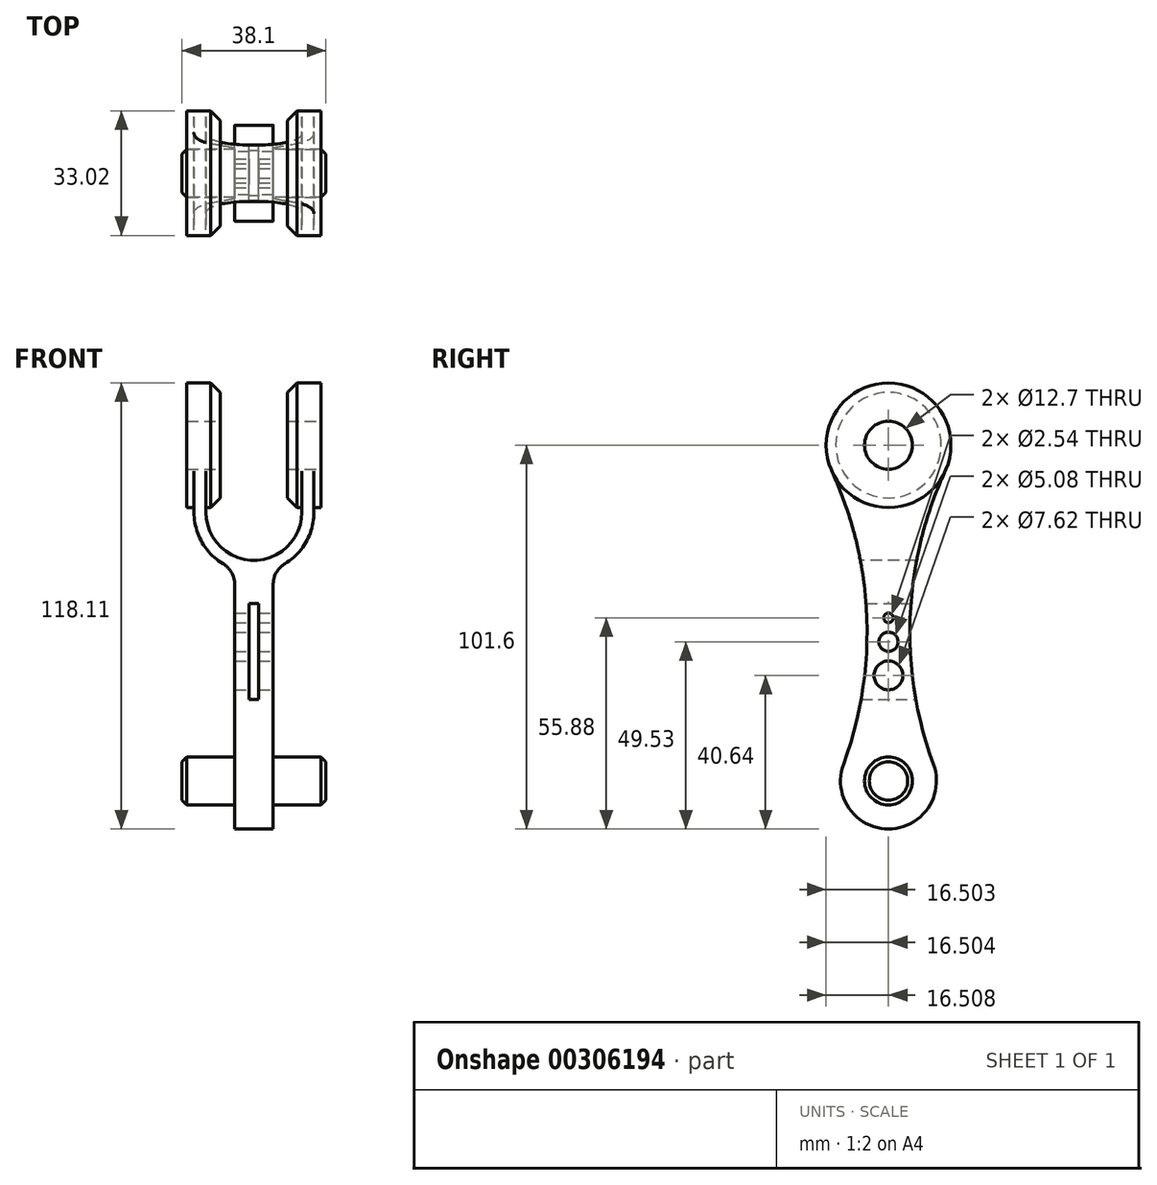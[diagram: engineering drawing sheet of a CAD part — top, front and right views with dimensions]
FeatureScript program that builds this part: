
annotation { "Feature Type Name" : "Feature", "Feature Type Description" : "" }
export const myFeature = defineFeature(function(context is Context, id is Id, definition is map)
    precondition{}
    {
        {
            var Q0;
            Q0=qCreatedBy(makeId("Front.planeOp"),FACE);
            var sketch = newSketch(context, id + "F0", { "sketchPlane" : qUnion([Q0])});
            skPoint(sketch, "E0.middle", {"position": v(0, 0) * mm});
            skArc(sketch, "E1", {"start": v(-8.17, -19.4) * mm, "mid": v(-13.82, -25.2) * mm, "end": v(-15.88, -33.02) * mm});
            skLineSegment(sketch, "E2.bottom", {"start": v(-5.08, 15.05) * mm, "end": v(5.08, 15.05) * mm});
            skLineSegment(sketch, "E2.left", {"start": v(-5.08, 15.05) * mm, "end": v(-5.08, -13.95) * mm});
            skLineSegment(sketch, "E2.right", {"start": v(5.08, 15.05) * mm, "end": v(5.08, -13.95) * mm});
            skArc(sketch, "E3", {"start": v(12.7, -33.02) * mm, "mid": v(0, -20.32) * mm, "end": v(-12.7, -33.02) * mm});
            skLineSegment(sketch, "E4.top", {"start": v(14.22, -50.8) * mm, "end": v(14.36, -50.8) * mm});
            skLineSegment(sketch, "E4.left", {"start": v(12.7, -33.02) * mm, "end": v(12.7, -49.28) * mm});
            skLineSegment(sketch, "E4.right", {"start": v(15.88, -33.02) * mm, "end": v(15.88, -49.28) * mm});
            skLineSegment(sketch, "E5.top", {"start": v(-14.36, -50.8) * mm, "end": v(-14.22, -50.8) * mm});
            skLineSegment(sketch, "E5.left", {"start": v(-15.88, -33.02) * mm, "end": v(-15.88, -49.28) * mm});
            skLineSegment(sketch, "E5.right", {"start": v(-12.7, -33.02) * mm, "end": v(-12.7, -49.28) * mm});
            skArc(sketch, "E6.trimOffspring", {"start": v(15.88, -33.02) * mm, "mid": v(13.82, -25.2) * mm, "end": v(8.17, -19.4) * mm});
            skPoint(sketch, "E7.visualSharp", {"position": v(-5.08, -17.97) * mm});
            skArc(sketch, "E7.filletArc", {"start": v(-8.17, -19.4) * mm, "mid": v(-5.9, -17.08) * mm, "end": v(-5.08, -13.95) * mm});
            skPoint(sketch, "E8.visualSharp", {"position": v(5.08, -17.97) * mm});
            skArc(sketch, "E8.filletArc", {"start": v(5.08, -13.95) * mm, "mid": v(5.9, -17.08) * mm, "end": v(8.17, -19.4) * mm});
            skArc(sketch, "E9.filletArc", {"start": v(12.7, -49.28) * mm, "mid": v(13.15, -50.35) * mm, "end": v(14.22, -50.8) * mm});
            skArc(sketch, "E10.filletArc", {"start": v(14.36, -50.8) * mm, "mid": v(15.44, -50.35) * mm, "end": v(15.88, -49.28) * mm});
            skArc(sketch, "E11.filletArc", {"start": v(-15.88, -49.28) * mm, "mid": v(-15.44, -50.35) * mm, "end": v(-14.36, -50.8) * mm});
            skArc(sketch, "E12.filletArc", {"start": v(-14.22, -50.8) * mm, "mid": v(-13.15, -50.35) * mm, "end": v(-12.7, -49.28) * mm});
            skSolve(sketch);
        }
        {
            var Q0;
            Q0=qSketchRegion(id+"F0",true);
            extrude(context, id + "F1", {"entities" : qUnion([Q0]), "depth" : 38.1 * mm, "symmetric" : true});
        }
        {
            var Q0;
            Q0=qCreatedBy(makeId("Right.planeOp"),FACE);
            var sketch = newSketch(context, id + "F2", { "sketchPlane" : qUnion([Q0])});
            skCircle(sketch, "E13", {"center": v(0, -50.8) * mm, "radius": 6.35 * mm});
            skSolve(sketch);
        }
        {
            var Q0;
            Q0=qCreatedBy(makeId("Right.planeOp"),FACE);
            var sketch = newSketch(context, id + "F3", { "sketchPlane" : qUnion([Q0])});
            skCircle(sketch, "E14", {"center": v(0, -50.8) * mm, "radius": 16.51 * mm});
            skSolve(sketch);
        }
        {
            var Q0;
            Q0=qSketchRegion(id+"F3",true);
            extrude(context, id + "F4", {"entities" : qUnion([Q0]), "operationType" : NewBodyOperationType.ADD, "depth" : 35.56 * mm, "symmetric" : true});
        }
        {
            var Q0;
            Q0=qCreatedBy(makeId("Front.planeOp"),FACE);
            var sketch = newSketch(context, id + "F5", { "sketchPlane" : qUnion([Q0])});
            skLineSegment(sketch, "E15.bottom", {"start": v(8.9, -69.85) * mm, "end": v(-8.89, -69.85) * mm});
            skLineSegment(sketch, "E15.top", {"start": v(8.9, -31.75) * mm, "end": v(-8.89, -31.75) * mm});
            skLineSegment(sketch, "E15.left", {"start": v(8.9, -69.85) * mm, "end": v(8.9, -31.75) * mm});
            skLineSegment(sketch, "E15.right", {"start": v(-8.89, -69.85) * mm, "end": v(-8.89, -31.75) * mm});
            skPoint(sketch, "E15.middle", {"position": v(0, -50.8) * mm});
            skSolve(sketch);
        }
        {
            var Q0;
            Q0=qSketchRegion(id+"F2",true);
            extrude(context, id + "F6", {"entities" : qUnion([Q0]), "operationType" : NewBodyOperationType.REMOVE, "oppositeDirection" : true, "depth" : 76.2 * mm, "symmetric" : true});
        }
        {
            var Q0;
            Q0=qSketchRegion(id+"F5",true);
            extrude(context, id + "F7", {"entities" : qUnion([Q0]), "operationType" : NewBodyOperationType.REMOVE, "oppositeDirection" : true, "depth" : 38.1 * mm, "symmetric" : true});
        }
        {
            var Q0;
            Q0=makeQuery(id+"F7.boolean.opBoolean","INTERSECT",EDGE,{"derivedFrom":[makeQuery(id+"F4.opExtrude","SWEPT_FACE",FACE,{"disambiguationData":[OSD([sQuery(id+"F3.wireOp",EDGE,"E14")])]}),makeQuery(id+"F7.opExtrude","SWEPT_FACE",FACE,{"disambiguationData":[OSD([sQuery(id+"F5.wireOp",EDGE,"E15.right")])]})]});
            var Q1;
            Q1=makeQuery(id+"F7.boolean.opBoolean","INTERSECT",EDGE,{"derivedFrom":[makeQuery(id+"F4.opExtrude","SWEPT_FACE",FACE,{"disambiguationData":[OSD([sQuery(id+"F3.wireOp",EDGE,"E14")])]}),makeQuery(id+"F7.opExtrude","SWEPT_FACE",FACE,{"disambiguationData":[OSD([sQuery(id+"F5.wireOp",EDGE,"E15.left")])]})]});
            chamfer(context, id + "F8", {"entities" : qUnion([Q0, Q1]), "width" : 2.54 * mm, "tangentPropagation" : true});
        }
        {
            var Q0;
            Q0=qCreatedBy(makeId("Right.planeOp"),FACE);
            var sketch = newSketch(context, id + "F9", { "sketchPlane" : qUnion([Q0])});
            skArc(sketch, "E16", {"start": v(19.05, 38.09) * mm, "mid": v(0, 57.15) * mm, "end": v(-19.05, 38.09) * mm});
            skLineSegment(sketch, "E17.top", {"start": v(-19.05, 12.69) * mm, "end": v(19.05, 12.69) * mm});
            skLineSegment(sketch, "E17.left", {"start": v(-19.05, 38.09) * mm, "end": v(-19.05, 12.69) * mm});
            skLineSegment(sketch, "E17.right", {"start": v(19.05, 38.09) * mm, "end": v(19.05, 12.69) * mm});
            skSolve(sketch);
        }
        {
            var Q0;
            Q0=qSketchRegion(id+"F9",true);
            extrude(context, id + "F10", {"entities" : qUnion([Q0]), "operationType" : NewBodyOperationType.ADD, "depth" : 10.16 * mm, "symmetric" : true});
        }
        {
            var Q0;
            Q0=qCreatedBy(makeId("Right.planeOp"),FACE);
            var sketch = newSketch(context, id + "F11", { "sketchPlane" : qUnion([Q0])});
            skCircle(sketch, "E18", {"center": v(0, 38.1) * mm, "radius": 6.35 * mm});
            skSolve(sketch);
        }
        {
            var Q0;
            Q0=qSketchRegion(id+"F11",true);
            extrude(context, id + "F12", {"entities" : qUnion([Q0]), "operationType" : NewBodyOperationType.ADD, "depth" : 38.1 * mm, "symmetric" : true});
        }
        {
            var Q0;
            Q0=makeQuery(id+"F12.opExtrude","CAP_EDGE",EDGE,{"disambiguationData":[OSD([sQuery(id+"F11.wireOp",EDGE,"E18")])],"isStart":true});
            var Q1;
            Q1=makeQuery(id+"F12.opExtrude","CAP_EDGE",EDGE,{"disambiguationData":[OSD([sQuery(id+"F11.wireOp",EDGE,"E18")])],"isStart":false});
            chamfer(context, id + "F13", {"entities" : qUnion([Q0, Q1]), "width" : 1.27 * mm, "tangentPropagation" : true});
        }
        {
            var Q0;
            Q0=qCreatedBy(makeId("Right.planeOp"),FACE);
            var sketch = newSketch(context, id + "F14", { "sketchPlane" : qUnion([Q0])});
            skArc(sketch, "E19", {"start": v(11.92, 33.71) * mm, "mid": v(0, 50.8) * mm, "end": v(-11.92, 33.71) * mm});
            skArc(sketch, "E20", {"start": v(-15, -43.9) * mm, "mid": v(0, -67.31) * mm, "end": v(15, -43.9) * mm});
            skArc(sketch, "E21", {"start": v(11.92, 33.71) * mm, "mid": v(5.75, -5.4) * mm, "end": v(15, -43.9) * mm});
            skPoint(sketch, "E22.center.orphan", {"position": v(45.72, -6.35) * mm});
            skPoint(sketch, "E23.center.orphan", {"position": v(-45.72, -6.35) * mm});
            skArc(sketch, "E24", {"start": v(-15, -43.9) * mm, "mid": v(-5.75, -5.4) * mm, "end": v(-11.92, 33.71) * mm});
            skSolve(sketch);
        }
        {
            var Q0;
            Q0=qSketchRegion(id+"F14",true);
            extrude(context, id + "F15", {"entities" : qUnion([Q0]), "operationType" : NewBodyOperationType.INTERSECT, "depth" : 76.2 * mm, "symmetric" : true});
        }
        {
            var Q0;
            Q0=qCreatedBy(makeId("Front.planeOp"),FACE);
            var sketch = newSketch(context, id + "F16", { "sketchPlane" : qUnion([Q0])});
            skLineSegment(sketch, "E25.bottom", {"start": v(-1.27, -8.87) * mm, "end": v(1.27, -8.87) * mm});
            skLineSegment(sketch, "E25.top", {"start": v(-1.27, 16.53) * mm, "end": v(1.27, 16.53) * mm});
            skLineSegment(sketch, "E25.left", {"start": v(-1.27, -8.87) * mm, "end": v(-1.27, 16.53) * mm});
            skLineSegment(sketch, "E25.right", {"start": v(1.27, -8.87) * mm, "end": v(1.27, 16.53) * mm});
            skSolve(sketch);
        }
        {
            var Q0;
            Q0=qSketchRegion(id+"F16",true);
            extrude(context, id + "F17", {"entities" : qUnion([Q0]), "operationType" : NewBodyOperationType.REMOVE, "oppositeDirection" : true, "depth" : 50.8 * mm, "symmetric" : true});
        }
        {
            var Q0;
            Q0=qCreatedBy(makeId("Right.planeOp"),FACE);
            var sketch = newSketch(context, id + "F18", { "sketchPlane" : qUnion([Q0])});
            skCircle(sketch, "E26", {"center": v(0, 10.16) * mm, "radius": 3.81 * mm});
            skCircle(sketch, "E27", {"center": v(0, 1.27) * mm, "radius": 2.54 * mm});
            skCircle(sketch, "E28", {"center": v(0, -5.08) * mm, "radius": 1.27 * mm});
            skSolve(sketch);
        }
        {
            var Q0;
            Q0=qSketchRegion(id+"F18",true);
            extrude(context, id + "F19", {"entities" : qUnion([Q0]), "operationType" : NewBodyOperationType.REMOVE, "oppositeDirection" : true, "depth" : 25.4 * mm, "symmetric" : true});
        }
        {
            var Q0;
            Q0=makeQuery(id+"F1.opExtrude","SWEPT_BODY",BODY,{"disambiguationData":[OSD([sQuery(id+"F0.wireOp",EDGE,"E1"),sQuery(id+"F0.wireOp",EDGE,"E2.bottom"),sQuery(id+"F0.wireOp",EDGE,"E2.left"),sQuery(id+"F0.wireOp",EDGE,"E2.right"),sQuery(id+"F0.wireOp",EDGE,"E3"),sQuery(id+"F0.wireOp",EDGE,"E4.top"),sQuery(id+"F0.wireOp",EDGE,"E4.left"),sQuery(id+"F0.wireOp",EDGE,"E4.right"),sQuery(id+"F0.wireOp",EDGE,"E5.top"),sQuery(id+"F0.wireOp",EDGE,"E5.left"),sQuery(id+"F0.wireOp",EDGE,"E5.right"),sQuery(id+"F0.wireOp",EDGE,"E6.trimOffspring"),sQuery(id+"F0.wireOp",EDGE,"E7.filletArc"),sQuery(id+"F0.wireOp",EDGE,"E8.filletArc"),sQuery(id+"F0.wireOp",EDGE,"E9.filletArc"),sQuery(id+"F0.wireOp",EDGE,"E10.filletArc"),sQuery(id+"F0.wireOp",EDGE,"E11.filletArc"),sQuery(id+"F0.wireOp",EDGE,"E12.filletArc")])]});
            var Q1;
            {var subQ0=sQuery(id+"F11.wireOp",EDGE,"E18");Q1=makeQuery(id+"F13.opChamfer","BLEND_EDGE",EDGE,{"blendedFrom":[makeQuery(id+"F12.opExtrude","CAP_EDGE",EDGE,{"disambiguationData":[OSD([subQ0])],"isStart":false}),makeQuery(id+"F12.opExtrude","CAP_FACE",FACE,{"disambiguationData":[OSD([subQ0])],"isStart":false})],"blendedInto":[makeQuery(id+"F12.opExtrude","CAP_FACE",FACE,{"disambiguationData":[OSD([subQ0])],"isStart":false})]});}
            transform(context, id + "F20", {"entities" : qUnion([Q0]), "transformType" : TransformType.ROTATION, "transformAxis" : qUnion([Q1]), "angle" : 3.14 * radian, "makeCopy" : false});
        }
        {
            var Q0;
            Q0=qCreatedBy(makeId("Front.planeOp"),FACE);
            var sketch = newSketch(context, id + "F21", { "sketchPlane" : qUnion([Q0])});
            skPoint(sketch, "E29", {"position": v(-17.78, 127) * mm});
            skLineSegment(sketch, "E30", {"start": v(-17.78, 127) * mm, "end": v(17.78, 127) * mm});
            skPoint(sketch, "E31", {"position": v(0, 127) * mm});
            skLineSegment(sketch, "E32", {"start": v(0, 127) * mm, "end": v(0, 0) * mm, "construction": true});
            skSolve(sketch);
        }
        {
            var Q0;
            Q0=makeQuery(id+"F1.opExtrude","SWEPT_BODY",BODY,{"disambiguationData":[OSD([sQuery(id+"F0.wireOp",EDGE,"E1"),sQuery(id+"F0.wireOp",EDGE,"E2.bottom"),sQuery(id+"F0.wireOp",EDGE,"E2.left"),sQuery(id+"F0.wireOp",EDGE,"E2.right"),sQuery(id+"F0.wireOp",EDGE,"E3"),sQuery(id+"F0.wireOp",EDGE,"E4.top"),sQuery(id+"F0.wireOp",EDGE,"E4.left"),sQuery(id+"F0.wireOp",EDGE,"E4.right"),sQuery(id+"F0.wireOp",EDGE,"E5.top"),sQuery(id+"F0.wireOp",EDGE,"E5.left"),sQuery(id+"F0.wireOp",EDGE,"E5.right"),sQuery(id+"F0.wireOp",EDGE,"E6.trimOffspring"),sQuery(id+"F0.wireOp",EDGE,"E7.filletArc"),sQuery(id+"F0.wireOp",EDGE,"E8.filletArc"),sQuery(id+"F0.wireOp",EDGE,"E9.filletArc"),sQuery(id+"F0.wireOp",EDGE,"E10.filletArc"),sQuery(id+"F0.wireOp",EDGE,"E11.filletArc"),sQuery(id+"F0.wireOp",EDGE,"E12.filletArc")])]});
            var Q1;
            Q1=sQuery(id+"F21.wireOp",EDGE,"E32");
            transform(context, id + "F22", {"entities" : qUnion([Q0]), "transformType" : TransformType.TRANSLATION_ENTITY, "oppositeDirectionEntity" : false, "transformLine" : qUnion([Q1]), "makeCopy" : false});
        }
    });
